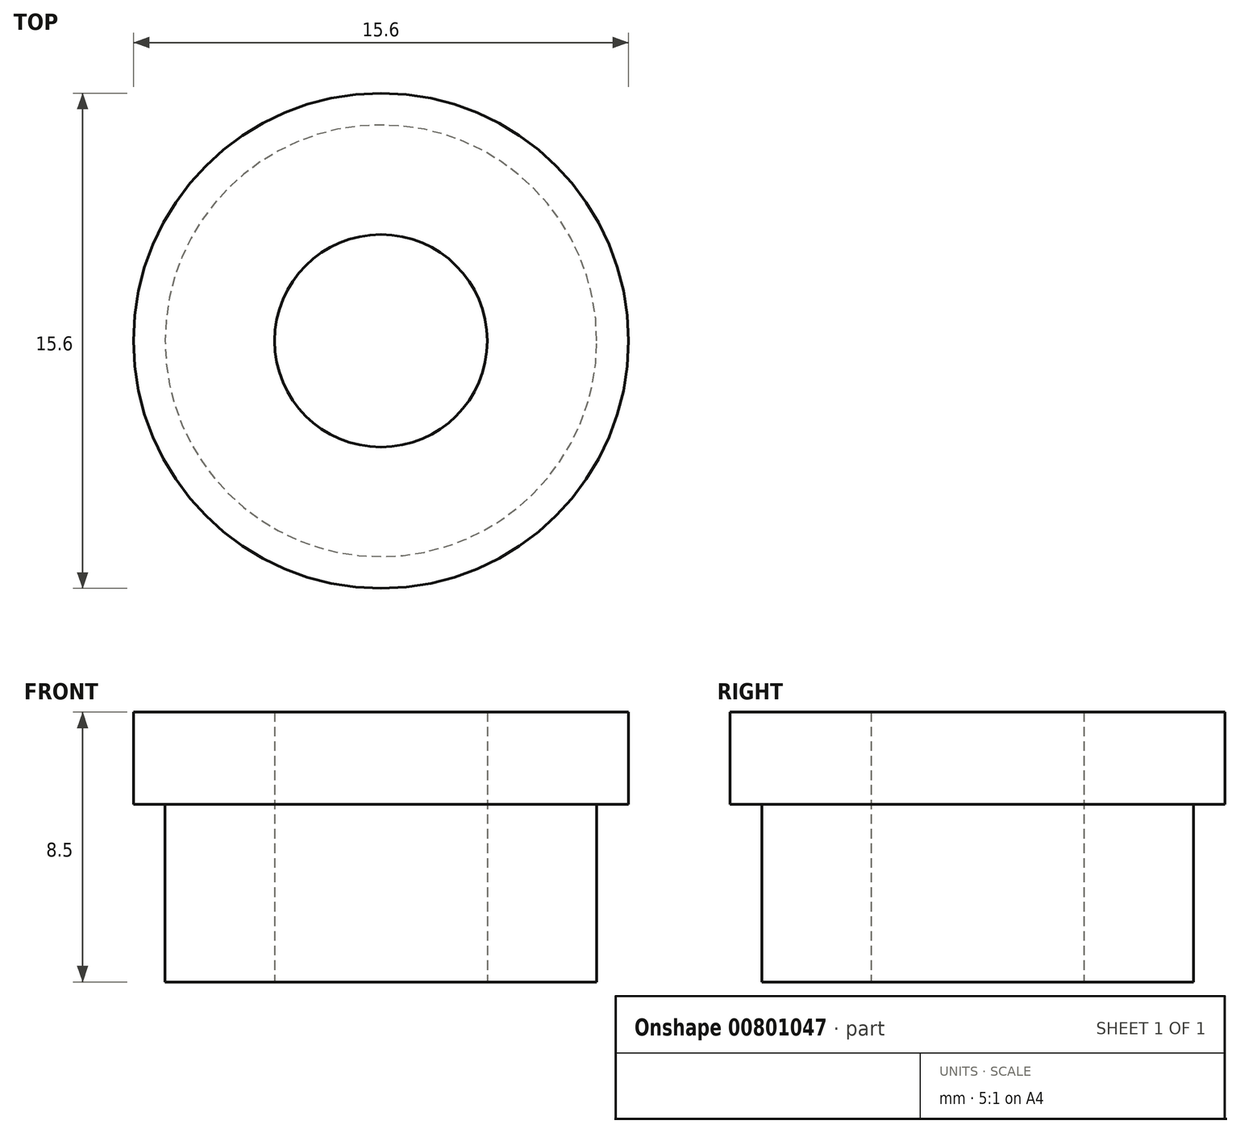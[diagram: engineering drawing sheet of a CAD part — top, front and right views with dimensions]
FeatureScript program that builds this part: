
annotation { "Feature Type Name" : "Feature", "Feature Type Description" : "" }
export const myFeature = defineFeature(function(context is Context, id is Id, definition is map)
    precondition{}
    {
        {
            var Q0;
            Q0=qCreatedBy(makeId("Front.planeOp"),FACE);
            var sketch = newSketch(context, id + "F0", { "sketchPlane" : qUnion([Q0])});
            skLineSegment(sketch, "E0", {"start": v(0, 0) * mm, "end": v(0, -8.5) * mm});
            skLineSegment(sketch, "E1", {"start": v(0, -8.5) * mm, "end": v(6.8, -8.5) * mm});
            skLineSegment(sketch, "E2", {"start": v(6.8, -8.5) * mm, "end": v(6.8, -2.9) * mm});
            skLineSegment(sketch, "E3", {"start": v(6.8, -2.9) * mm, "end": v(7.8, -2.9) * mm});
            skLineSegment(sketch, "E4", {"start": v(7.8, -2.9) * mm, "end": v(7.8, 0) * mm});
            skLineSegment(sketch, "E5", {"start": v(7.8, 0) * mm, "end": v(0, 0) * mm});
            skSolve(sketch);
        }
        {
            var Q0;
            Q0=makeQuery(id+"F0.imprint","IMPRINT",FACE,{"disambiguationData":[TD([[makeQuery(id+"F0.imprint","IMPRINT",EDGE,{"derivedFrom":sQuery(id+"F0.wireOp",EDGE,"E0")}),1.0]])]});
            var Q1;
            Q1=sQuery(id+"F0.wireOp",EDGE,"E0");
            revolve(context, id + "F1", {"surfaceOperationType" : NewSurfaceOperationType.NEW, "entities" : qUnion([Q0]), "axis" : qUnion([Q1]), "revolveType" : RevolveType.FULL});
        }
        {
            var Q0;
            Q0=makeQuery(id+"F1.opRevolve","SWEPT_FACE",FACE,{"disambiguationData":[OSD([sQuery(id+"F0.wireOp",EDGE,"E1")])]});
            cPlane(context, id + "F2", {"entities" : qUnion([Q0]), "cplaneType" : CPlaneType.OFFSET, "offset" : 0 * mm, "width" : 150 * mm, "height" : 150 * mm});
        }
        {
            var Q0;
            Q0=qCreatedBy(id+"F2.planeOp",FACE);
            var sketch = newSketch(context, id + "F3", { "sketchPlane" : qUnion([Q0])});
            skCircle(sketch, "E6", {"center": v(0, 0) * mm, "radius": 3.35 * mm});
            skSolve(sketch);
        }
        {
            var Q0;
            Q0=makeQuery(id+"F3.imprint","IMPRINT",FACE,{"disambiguationData":[TD([[makeQuery(id+"F3.imprint","IMPRINT",EDGE,{"derivedFrom":sQuery(id+"F3.wireOp",EDGE,"E6")}),1.0]])]});
            extrude(context, id + "F4", {"entities" : qUnion([Q0]), "operationType" : NewBodyOperationType.REMOVE, "endBound" : BoundingType.THROUGH_ALL, "oppositeDirection" : true, "depth" : 25 * mm, "offsetDistance" : 25 * mm});
        }
    });
